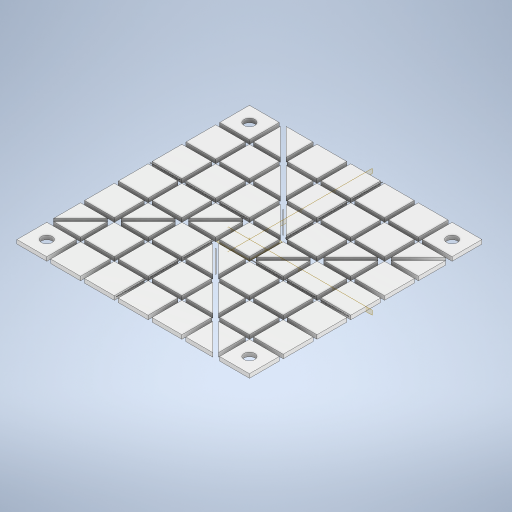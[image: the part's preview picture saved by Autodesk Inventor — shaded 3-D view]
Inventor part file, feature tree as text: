
AUTODESK INVENTOR PART (.ipt)
format: ipt  version: 2024 (Build 280153000, 153)  size: 687,104 bytes
history: native  units: in
note: dims shown in document units (in); Inventor stores cm internally (conversion verified against a paired STEP export)
features: extrude x4, sketch x3, plane x3, other x1, pattern_circular x1
ambient origin geometry x8: Origin, YZ Plane, XZ Plane, XY Plane, X Axis, Y Axis, Z Axis, Center Point
bodies: Solid1 (feature_tree)
feature tree (12):
  sketch  "Sketch1"  dims[d0=3.75in d1=3.75in]
  extrude  "Extrusion1"  Depth=3.75in
  extrude  "Extrusion2"  Depth=0.5357in
  other  "Work Axis1"
  pattern_circular  "Circular Pattern1"  [2 undecoded]
  sketch  "Sketch3"  dims[d2=3.1496in d4=0.5357in d5=3.1496in d7=0.5357in d10=0.0312in]
  sketch  "Sketch4"  dims[d11=0.0312in d12=0.0312in d13=0.0312in d14=0.0312in d15=0.0312in d16=0.0312in d17=0.0312in d18=0.0312in d19=0.0312in d20=0.0312in d21=0.0312in d22=0.0312in d23=0.0312in d24=0.0312in d25=0.0312in d26=0.0312in d27=0.0312in d28=0.0312in d29=0.0625in d30=0.0in d31=0.0625in d32=0.0in d33=1.5748in d34=360.0deg d36=0.17in d37=0.2679in d38=0.2679in d39=1.54in d40=0.01in d41=0.0025in d42=1.5748in d44=360.0deg d46=0.01in d47=0.5in d48=1.5748in d50=360.0deg d52=0.002in d53=0.0in d54=-0.0315in d55=0.002in d56=0.0in]
  extrude  "Extrusion3"  Depth=0.002in
  plane  "Work Plane3"
  extrude  "Extrusion4"  Depth=0.002in
  plane  "Work Plane1"
  plane  "Work Plane2"
note: 2 required parameter values undecoded (feature->parameter linkage not recoverable at this tier; creation-order binding heuristic only, values carry confidence <= 0.55)
